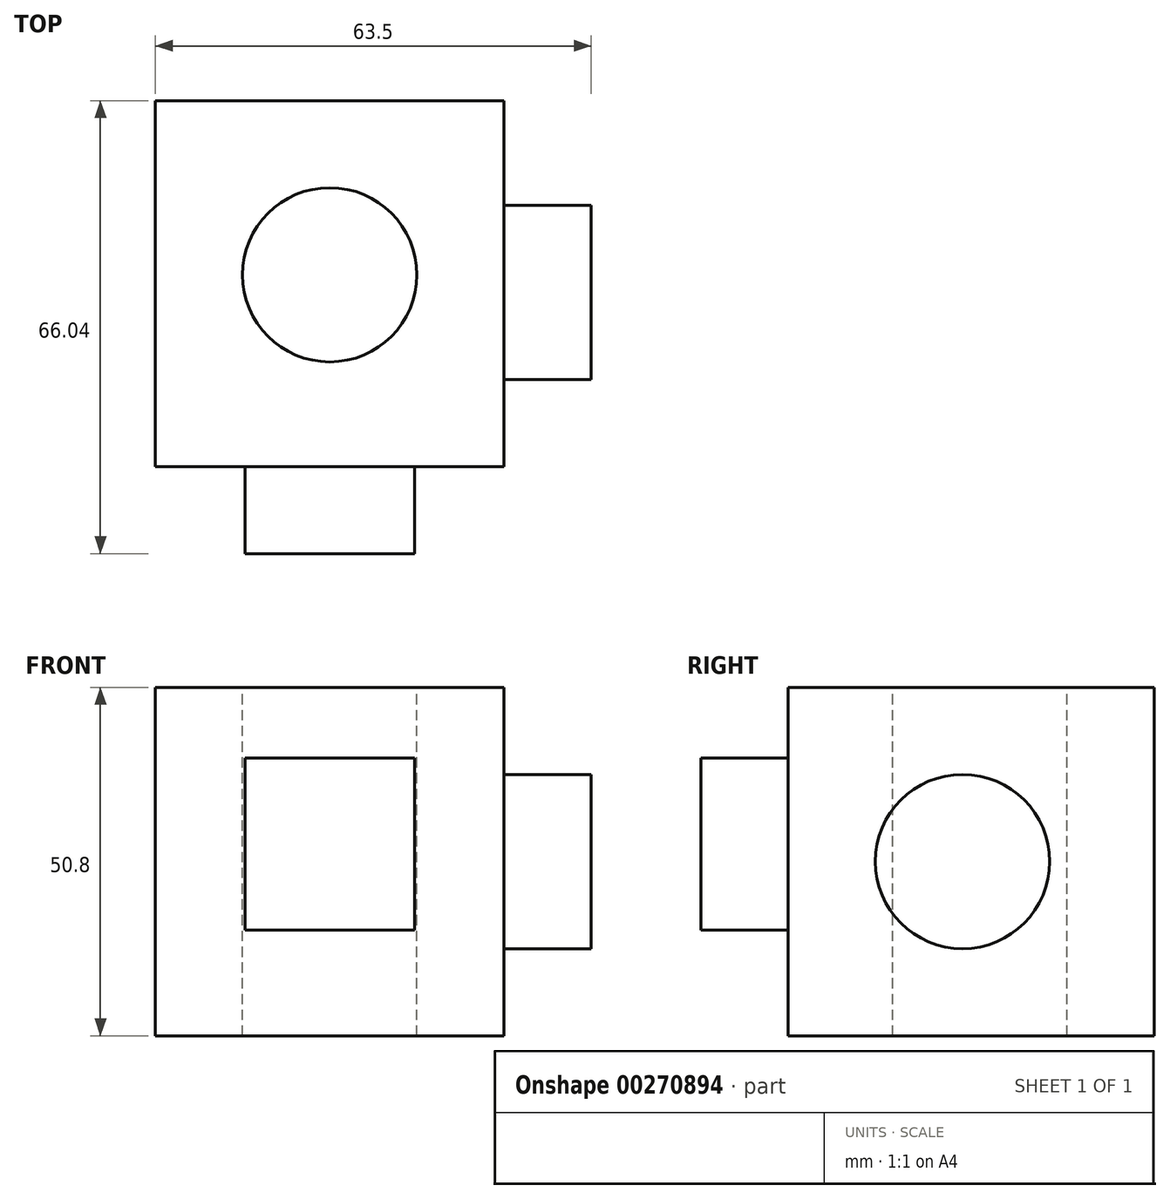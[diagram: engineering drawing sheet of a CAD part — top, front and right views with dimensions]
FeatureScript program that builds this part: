
annotation { "Feature Type Name" : "Feature", "Feature Type Description" : "" }
export const myFeature = defineFeature(function(context is Context, id is Id, definition is map)
    precondition{}
    {
        {
            var Q0;
            Q0=qCreatedBy(makeId("Front.planeOp"),FACE);
            var sketch = newSketch(context, id + "F0", { "sketchPlane" : qUnion([Q0])});
            skLineSegment(sketch, "E0.bottom", {"start": v(0, 0) * mm, "end": v(-50.8, 0) * mm});
            skLineSegment(sketch, "E0.top", {"start": v(0, 50.8) * mm, "end": v(-50.8, 50.8) * mm});
            skLineSegment(sketch, "E0.left", {"start": v(0, 0) * mm, "end": v(0, 50.8) * mm});
            skLineSegment(sketch, "E0.right", {"start": v(-50.8, 0) * mm, "end": v(-50.8, 50.8) * mm});
            skSolve(sketch);
        }
        {
            var Q0;
            Q0 = qSketchRegion(id + "F0", true);
            extrude(context, id + "F1", {"entities" : qUnion([Q0]), "depth" : 53.34 * mm});
        }
        {
            var Q0;
            Q0=makeQuery(id+"F1.opExtrude","SWEPT_FACE",FACE,{"disambiguationData":[OSD([sQuery(id+"F0.wireOp",EDGE,"E0.top")])]});
            var sketch = newSketch(context, id + "F2", { "sketchPlane" : qUnion([Q0])});
            skCircle(sketch, "E1", {"center": v(-25.4, -25.4) * mm, "radius": 12.7 * mm});
            skSolve(sketch);
        }
        {
            var Q0;
            Q0 = qSketchRegion(id + "F2", true);
            extrude(context, id + "F3", {"entities" : qUnion([Q0]), "operationType" : NewBodyOperationType.REMOVE, "oppositeDirection" : true, "depth" : 50.8 * mm});
        }
        {
            var Q0;
            Q0=makeQuery(id+"F1.opExtrude","CAP_FACE",FACE,{"disambiguationData":[OSD([sQuery(id+"F0.wireOp",EDGE,"E0.bottom"),sQuery(id+"F0.wireOp",EDGE,"E0.top"),sQuery(id+"F0.wireOp",EDGE,"E0.left"),sQuery(id+"F0.wireOp",EDGE,"E0.right")])],"isStart":false});
            var sketch = newSketch(context, id + "F4", { "sketchPlane" : qUnion([Q0])});
            skLineSegment(sketch, "E2.bottom", {"start": v(-13.06, 40.49) * mm, "end": v(-37.74, 40.49) * mm});
            skLineSegment(sketch, "E2.top", {"start": v(-13.06, 15.44) * mm, "end": v(-37.74, 15.44) * mm});
            skLineSegment(sketch, "E2.left", {"start": v(-13.06, 40.49) * mm, "end": v(-13.06, 15.44) * mm});
            skLineSegment(sketch, "E2.right", {"start": v(-37.74, 40.49) * mm, "end": v(-37.74, 15.44) * mm});
            skPoint(sketch, "E2.middle", {"position": v(-25.4, 27.96) * mm});
            skPoint(sketch, "E2.middle.positionSnap0", {"position": v(-25.4, 50.8) * mm});
            skPoint(sketch, "E2.centerSnap0", {"position": v(-25.4, 50.8) * mm});
            skSolve(sketch);
        }
        {
            var Q0;
            Q0=makeQuery(id+"F4.imprint","IMPRINT",FACE,{"disambiguationData":[TD([[makeQuery(id+"F4.imprint","IMPRINT",EDGE,{"derivedFrom":sQuery(id+"F4.wireOp",EDGE,"E2.bottom")}),1.0]])]});
            extrude(context, id + "F5", {"entities" : qUnion([Q0]), "operationType" : NewBodyOperationType.ADD, "depth" : 12.7 * mm});
        }
        {
            var Q0;
            Q0=makeQuery(id+"F1.opExtrude","SWEPT_FACE",FACE,{"disambiguationData":[OSD([sQuery(id+"F0.wireOp",EDGE,"E0.left")])]});
            var sketch = newSketch(context, id + "F6", { "sketchPlane" : qUnion([Q0])});
            skCircle(sketch, "E3", {"center": v(-27.94, 25.4) * mm, "radius": 12.7 * mm});
            skSolve(sketch);
        }
        {
            var Q0;
            Q0 = qSketchRegion(id + "F6", true);
            extrude(context, id + "F7", {"entities" : qUnion([Q0]), "operationType" : NewBodyOperationType.ADD, "depth" : 12.7 * mm});
        }
    });
